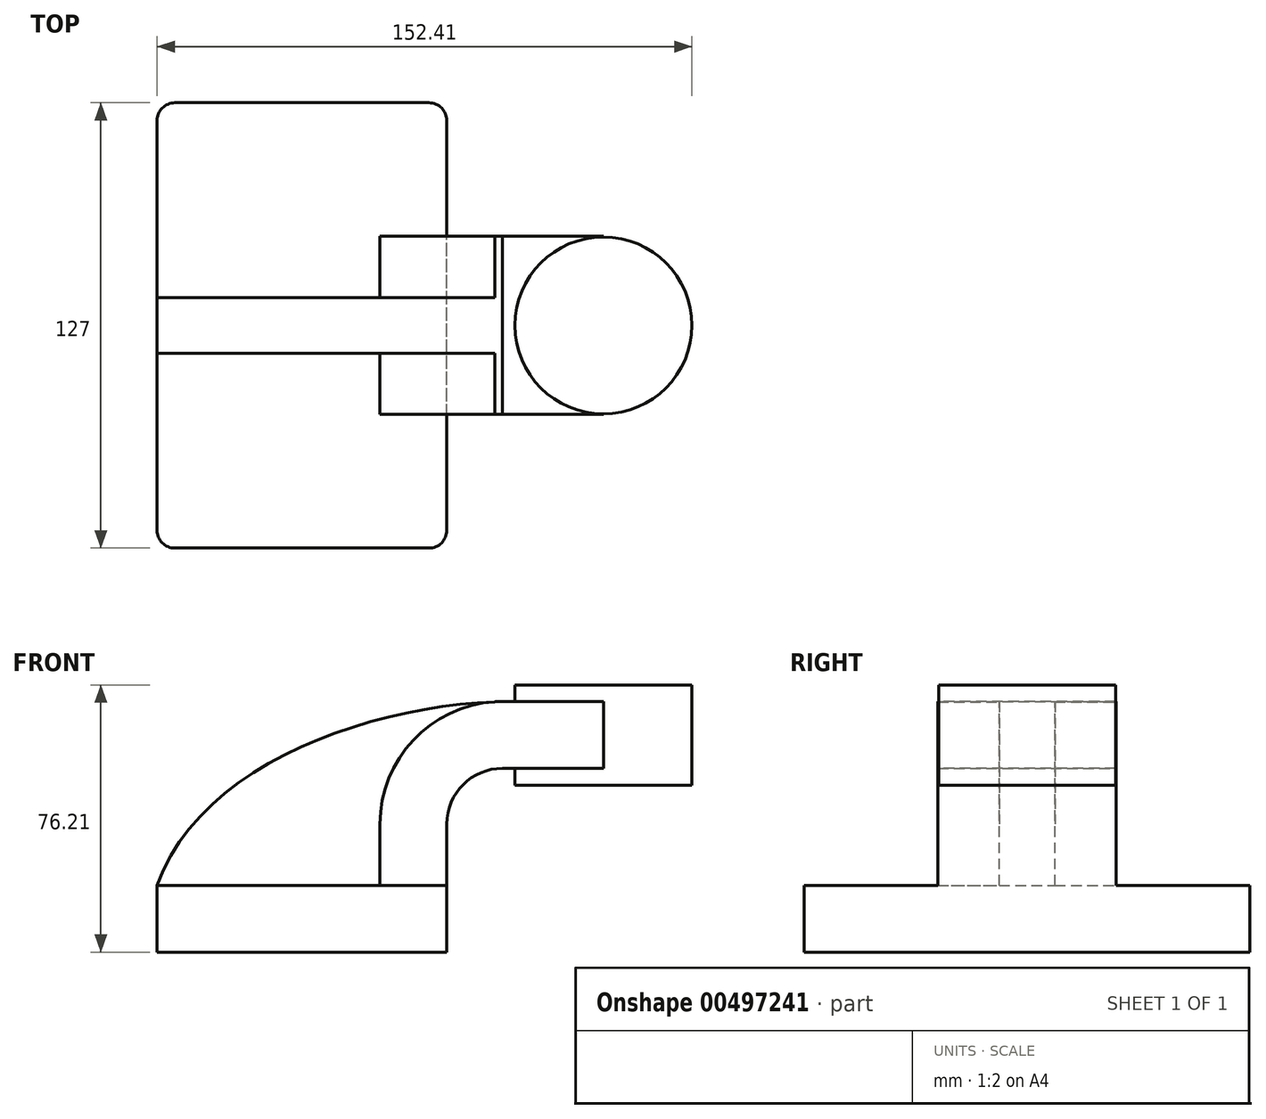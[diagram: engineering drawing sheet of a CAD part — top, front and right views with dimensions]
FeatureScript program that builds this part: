
annotation { "Feature Type Name" : "Feature", "Feature Type Description" : "" }
export const myFeature = defineFeature(function(context is Context, id is Id, definition is map)
    precondition{}
    {
        {
            var Q0;
            Q0=qCreatedBy(makeId("Front.planeOp"),FACE);
            var sketch = newSketch(context, id + "F0", { "sketchPlane" : qUnion([Q0])});
            skLineSegment(sketch, "E0.bottom", {"start": v(-41.27, 9.52) * mm, "end": v(41.28, 9.53) * mm});
            skLineSegment(sketch, "E0.top", {"start": v(-41.28, -9.52) * mm, "end": v(41.28, -9.52) * mm});
            skLineSegment(sketch, "E0.left", {"start": v(-41.28, 9.52) * mm, "end": v(-41.28, -9.52) * mm});
            skLineSegment(sketch, "E0.right", {"start": v(41.28, 9.53) * mm, "end": v(41.28, -9.52) * mm});
            skPoint(sketch, "E0.middle", {"position": v(0, 0) * mm});
            skLineSegment(sketch, "E1.bottom", {"start": v(60.32, 66.68) * mm, "end": v(111.12, 66.68) * mm});
            skLineSegment(sketch, "E1.top", {"start": v(60.32, 38.1) * mm, "end": v(111.12, 38.1) * mm});
            skLineSegment(sketch, "E1.left", {"start": v(60.32, 66.68) * mm, "end": v(60.32, 38.1) * mm});
            skLineSegment(sketch, "E1.right", {"start": v(111.12, 66.68) * mm, "end": v(111.13, 38.1) * mm});
            skPoint(sketch, "E1.middle", {"position": v(85.72, 52.39) * mm});
            skLineSegment(sketch, "E2", {"start": v(41.27, 9.53) * mm, "end": v(41.27, 27) * mm});
            skArc(sketch, "E3", {"start": v(41.27, 27) * mm, "mid": v(45.92, 38.23) * mm, "end": v(57.15, 42.88) * mm});
            skLineSegment(sketch, "E4", {"start": v(57.15, 42.88) * mm, "end": v(85.9, 42.88) * mm});
            skLineSegment(sketch, "E5.0", {"start": v(57.15, 61.93) * mm, "end": v(85.9, 61.93) * mm});
            skArc(sketch, "E5.1", {"start": v(22.22, 27) * mm, "mid": v(32.45, 51.7) * mm, "end": v(57.15, 61.93) * mm});
            skLineSegment(sketch, "E5.2", {"start": v(22.22, 9.53) * mm, "end": v(22.22, 27) * mm});
            skLineSegment(sketch, "E6", {"start": v(85.9, 61.93) * mm, "end": v(85.9, 42.88) * mm});
            skLineSegment(sketch, "E7", {"start": v(22.22, 9.53) * mm, "end": v(41.28, 9.53) * mm});
            skLineSegment(sketch, "E8", {"start": v(85.9, 42.88) * mm, "end": v(85.9, 38.1) * mm});
            skPoint(sketch, "E8.endSnap0", {"position": v(85.72, 38.1) * mm});
            skLineSegment(sketch, "E9", {"start": v(85.9, 61.93) * mm, "end": v(85.9, 66.68) * mm});
            skFitSpline(sketch, "E10", {"points": [v(-41.28, 9.53) * mm, v(57.15, 61.93) * mm], "startDerivative": vector(36.03, 103.36) * mm, "endDerivative": vector(112.5, 2.61) * mm});
            skSolve(sketch);
        }
        {
            var Q0;
            Q0=makeQuery(id+"F0.imprint","IMPRINT",FACE,{"disambiguationData":[TD([[makeQuery(id+"F0.imprint","IMPRINT",EDGE,{"derivedFrom":sQuery(id+"F0.wireOp",EDGE,"E0.bottom")}),-1.0]])]});
            extrude(context, id + "F1", {"entities" : qUnion([Q0]), "endBound" : BoundingType.SYMMETRIC, "depth" : 127 * mm});
        }
        {
            var Q0;
            Q0=makeQuery(id+"F0.imprint","IMPRINT",FACE,{"disambiguationData":[TD([[makeQuery(id+"F0.imprint","IMPRINT",EDGE,{"derivedFrom":sQuery(id+"F0.wireOp",EDGE,"E2")}),1.0]])]});
            var Q1;
            {var subQ5=sQuery(id+"F0.wireOp",EDGE,"E6");Q1=makeQuery(id+"F0.imprint","IMPRINT",FACE,{"disambiguationData":[TD([[makeQuery(id+"F0.imprint","IMPRINT",EDGE,{"derivedFrom":subQ5}),-1.0]])]});}
            extrude(context, id + "F2", {"entities" : qUnion([Q0, Q1]), "operationType" : NewBodyOperationType.ADD, "endBound" : BoundingType.SYMMETRIC, "depth" : 50.8 * mm});
        }
        {
            var Q0;
            {var subQ0=sQuery(id+"F0.wireOp",EDGE,"E0.bottom");Q0=makeQuery(id+"F0.imprint","IMPRINT",FACE,{"disambiguationData":[TD([[makeQuery(id+"F0.imprint","IMPRINT",EDGE,{"derivedFrom":subQ0}),1.0]])]});}
            extrude(context, id + "F3", {"entities" : qUnion([Q0]), "operationType" : NewBodyOperationType.ADD, "endBound" : BoundingType.SYMMETRIC, "depth" : 15.88 * mm});
        }
        {
            var Q0;
            {var subQ0=sQuery(id+"F0.wireOp",EDGE,"E1.right");Q0=makeQuery(id+"F0.imprint","IMPRINT",FACE,{"disambiguationData":[TD([[makeQuery(id+"F0.imprint","IMPRINT",EDGE,{"derivedFrom":subQ0}),-1.0]])]});}
            var Q1;
            Q1=sQuery(id+"F0.wireOp",EDGE,"E6");
            revolve(context, id + "F4", {"operationType" : NewBodyOperationType.ADD, "entities" : qUnion([Q0]), "axis" : qUnion([Q1]), "revolveType" : RevolveType.FULL});
        }
        {
            var Q0;
            Q0=makeQuery(id+"F1.opExtrude","CAP_EDGE",EDGE,{"disambiguationData":[OSD([sQuery(id+"F0.wireOp",EDGE,"E0.right")])],"isStart":false});
            var Q1;
            Q1=makeQuery(id+"F1.opExtrude","CAP_EDGE",EDGE,{"disambiguationData":[OSD([sQuery(id+"F0.wireOp",EDGE,"E0.left")])],"isStart":false});
            var Q2;
            Q2=makeQuery(id+"F1.opExtrude","CAP_EDGE",EDGE,{"disambiguationData":[OSD([sQuery(id+"F0.wireOp",EDGE,"E0.right")])],"isStart":true});
            var Q3;
            Q3=makeQuery(id+"F1.opExtrude","CAP_EDGE",EDGE,{"disambiguationData":[OSD([sQuery(id+"F0.wireOp",EDGE,"E0.left")])],"isStart":true});
            fillet(context, id + "F5", {"entities" : qUnion([Q0, Q1, Q2, Q3]), "radius" : 5.08 * mm, "tangentPropagation" : true, "allowEdgeOverflow" : false});
        }
    });
